# Revit family: 0046032_suspended
name_source: partatom
category: Lighting Fixtures
revit_build: Autodesk Revit 2016 (Build: 20150220_1215(x64)
units: mm (PartAtom-declared; Revit-internal decimal feet)

## family parameters
Cut with Voids When Loaded = No
Host = Face
Light Source = No
OmniClass Number = 23.80.70.00
OmniClass Title = Lighting
Part Type = Normal
Room Calculation Point = No
Round Connector Dimension = Use Diameter
Shared = No

## types (1)
- 0046032 ST WTRPRF SLIM 1500 IP65 6200LM 840
    Apparent Load = 50 VA
    Assembly Code = D5020200
    AssetType = Fixed
    BracketDistance_SYL = 750 mm  [stored 2.46063 ft]
    ClassificationName = Uniclass2015
    ClassificationValue = EF_70_80
    Cost = 0 $
    Default Elevation = 1219 mm
    Description = START Waterproof Slim is a LED integrated polycarbonate housing luminaire with easy to access electrical terminal through bayonet lock end caps and tool-free electrical connection due to push-in terminal. Flexible installation as mounting brackets can be positioned freely on the luminaire. 50W; 6500lm; High efficiency with 130lm/W and 50,000 lifetime. SDCM ≤6; IP65; IK08; Class I; 1489mm x 63mm x 75mm ,
    DocumentationLiterature = http://www.sylvania-lighting.com
    ElectricShockClassification = Class I
    IfcExportAs = IfcLightFixtureType
    IfcExportType = IfcLightFixtureType
    ImpactProtectionIndex = IK08
    IngressProtection = IP65
    Keynote = 16500
    Lamp = LED
    LampColourRenderingIndex = 80
    LampColourTemperature = 4000 K
    LampNominalLuminous = 6500 lm
    LampsType = LED
    LuminousEfficacy = 130 lm/W
    M_SYL = No
    Manufacturer = Feilo Sylvania
    ManufacturerName = Feilo Sylvania
    Material_1_SYL = PC/ABS Plastic
    Material_2_SYL = Diffuser-Sylvania
    Material_3_SYL = Aluminum
    Material_4_SYL = <By Category>
    Model = START Waterproof Slim 1500 IP65 6200lm 840
    ModelNumber = 0046032
    ModelReference = START Waterproof Slim 1500 IP65 6200lm 840
    Name = START Waterproof Slim 1500 IP65 6200lm 840
    NominalDepth = 63 mm  [stored 0.206693 ft]
    NominalHeight = 75 mm
    NominalLength = 1448 mm  [stored 4.75066 ft]
    PowerConsumption = 50 W
    PowerFactor = 0.9
    S_SYL = No
    Type Image = <None>
    TypeFixture_SYL = START Waterproof Slim Fixture : 0046032 ST WTRPRF SLIM 1500 IP65 6200LM 840
    TypeName = START Waterproof Slim 1500 IP65 6200lm 840
    URL = http://www.sylvania-lighting.com
    Voltage = 0 V
    Weight = 8.88 kg

note: [stored X ft] marks values corroborated as IEEE doubles in the binary element streams (Revit-internal decimal feet)

## geometry (parser evidence)
native form markers: Sweep x5
no freeform markers — native parametric forms only
